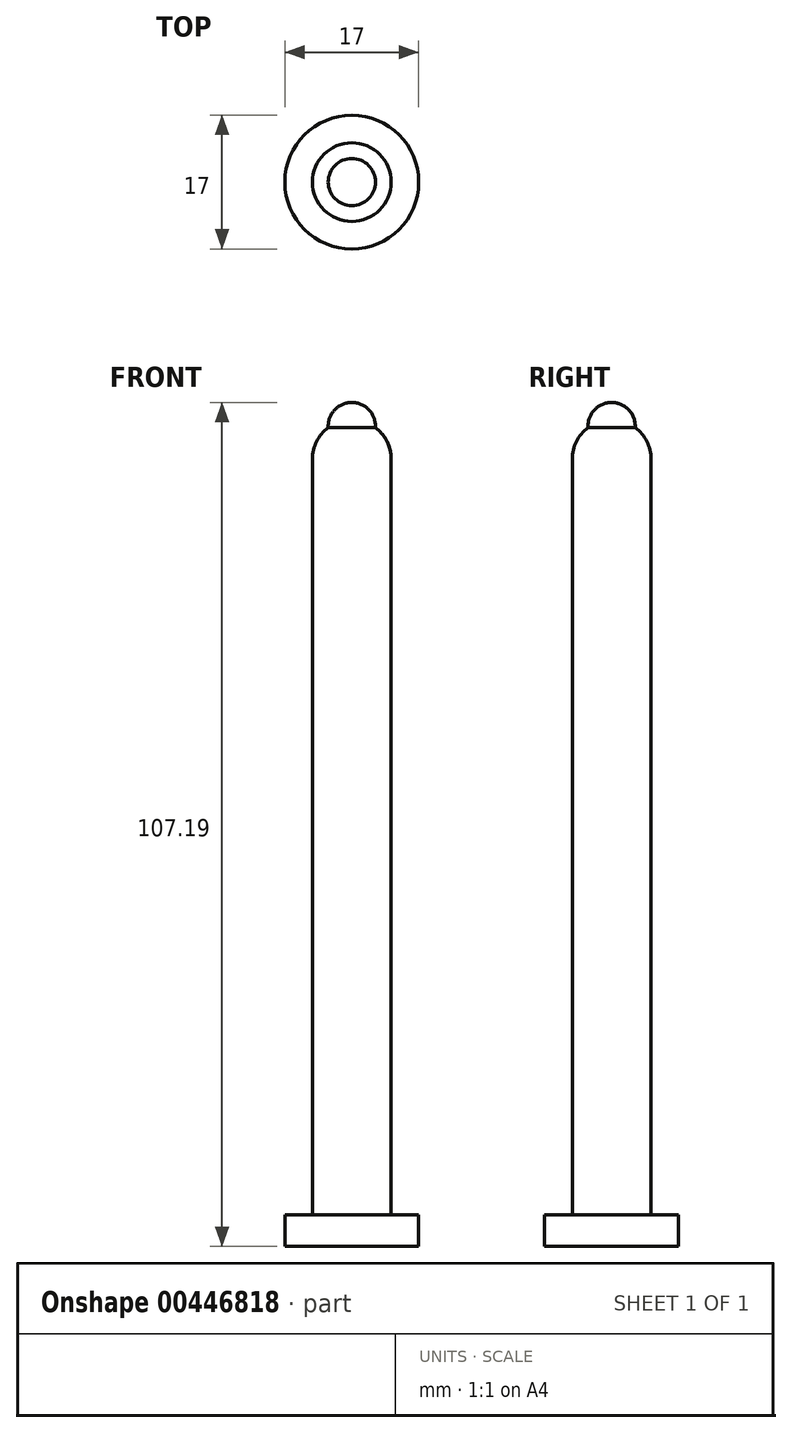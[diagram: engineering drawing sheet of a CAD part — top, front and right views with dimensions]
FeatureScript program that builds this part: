
annotation { "Feature Type Name" : "Feature", "Feature Type Description" : "" }
export const myFeature = defineFeature(function(context is Context, id is Id, definition is map)
    precondition{}
    {
        {
            var Q0;
            Q0=qCreatedBy(makeId("Top.planeOp"),FACE);
            var sketch = newSketch(context, id + "F0", { "sketchPlane" : qUnion([Q0])});
            skCircle(sketch, "E0", {"center": v(0, 0) * mm, "radius": 8.5 * mm});
            skSolve(sketch);
        }
        {
            var Q0;
            Q0=qSketchRegion(id+"F0",true);
            extrude(context, id + "F1", {"entities" : qUnion([Q0]), "depth" : 4 * mm});
        }
        {
            var Q0;
            Q0=qCreatedBy(makeId("Top.planeOp"),FACE);
            var sketch = newSketch(context, id + "F2", { "sketchPlane" : qUnion([Q0])});
            skCircle(sketch, "E1", {"center": v(0, 0) * mm, "radius": 5 * mm});
            skSolve(sketch);
        }
        {
            var Q0;
            Q0=qSketchRegion(id+"F2",true);
            extrude(context, id + "F3", {"entities" : qUnion([Q0]), "operationType" : NewBodyOperationType.ADD, "depth" : 100 * mm});
        }
        {
            var Q0;
            Q0=qCreatedBy(makeId("Right.planeOp"),FACE);
            var sketch = newSketch(context, id + "F4", { "sketchPlane" : qUnion([Q0])});
            skLineSegment(sketch, "E2", {"start": v(0, 100) * mm, "end": v(5, 100) * mm});
            skArc(sketch, "E3", {"start": v(5, 100) * mm, "mid": v(3.54, 103.54) * mm, "end": v(0, 105) * mm});
            skLineSegment(sketch, "E4", {"start": v(3, 104) * mm, "end": v(0, 104) * mm});
            skArc(sketch, "E5", {"start": v(3, 104) * mm, "mid": v(2.19, 106.24) * mm, "end": v(0, 107.19) * mm});
            skLineSegment(sketch, "E6", {"start": v(0, 107.19) * mm, "end": v(0, 100) * mm});
            skSolve(sketch);
        }
        {
            var Q0;
            {var subQ0=sQuery(id+"F4.wireOp",EDGE,"E2");Q0=makeQuery(id+"F4.imprint","IMPRINT",FACE,{"disambiguationData":[TD([[makeQuery(id+"F4.imprint","IMPRINT",EDGE,{"derivedFrom":subQ0}),1.0]])]});}
            var Q1;
            {var subQ3=sQuery(id+"F4.wireOp",EDGE,"E5");Q1=makeQuery(id+"F4.imprint","IMPRINT",FACE,{"disambiguationData":[TD([[makeQuery(id+"F4.imprint","IMPRINT",EDGE,{"derivedFrom":subQ3}),1.0]])]});}
            var Q2;
            {var subQ0=sQuery(id+"F4.wireOp",EDGE,"E6");var subQ1=sQuery(id+"F4.wireOp",EDGE,"E3");var subQ2=makeQuery(id+"F4.imprint","INTERSECT",VERTEX,{"derivedFrom":[subQ1,subQ0]});Q2=makeQuery(id+"F4.imprint","IMPRINT",FACE,{"disambiguationData":[TD([[makeQuery(id+"F4.imprint","IMPRINT",EDGE,{"disambiguationData":[TD([[subQ2,-1.0]])],"derivedFrom":subQ0}),1.0]])]});}
            var Q3;
            Q3=sQuery(id+"F4.wireOp",EDGE,"E6");
            revolve(context, id + "F5", {"operationType" : NewBodyOperationType.ADD, "entities" : qUnion([Q0, Q1, Q2]), "axis" : qUnion([Q3]), "revolveType" : RevolveType.FULL});
        }
    });
